annotation { "Feature Type Name" : "Feature", "Feature Type Description" : "" }
export const myFeature = defineFeature(function(context is Context, id is Id, definition is map)
    precondition{}
    {
        {
            var Q0;
            Q0=qCreatedBy(makeId("Top.planeOp"),FACE);
            var sketch = newSketch(context, id + "F0", { "sketchPlane" : qUnion([Q0])});
            skLineSegment(sketch, "E0.bottom", {"start": v(65.08, 7.73) * mm, "end": v(-14.92, 7.73) * mm});
            skLineSegment(sketch, "E0.top", {"start": v(65.08, 9.73) * mm, "end": v(-14.92, 9.73) * mm});
            skLineSegment(sketch, "E0.left", {"start": v(65.08, 7.73) * mm, "end": v(65.08, 9.73) * mm});
            skLineSegment(sketch, "E0.right", {"start": v(-14.92, 7.73) * mm, "end": v(-14.92, 9.73) * mm});
            skLineSegment(sketch, "E1", {"start": v(65.08, 9.73) * mm, "end": v(67.86, 29.54) * mm});
            skLineSegment(sketch, "E2", {"start": v(67.86, 29.54) * mm, "end": v(63.86, 29.54) * mm});
            skLineSegment(sketch, "E3", {"start": v(63.86, 29.54) * mm, "end": v(61.77, 14.68) * mm});
            skLineSegment(sketch, "E4", {"start": v(61.77, 14.68) * mm, "end": v(59.77, 14.68) * mm});
            skLineSegment(sketch, "E5", {"start": v(59.77, 14.68) * mm, "end": v(61.3, 25.58) * mm});
            skLineSegment(sketch, "E6", {"start": v(61.3, 25.58) * mm, "end": v(57.3, 25.58) * mm});
            skLineSegment(sketch, "E7", {"start": v(57.3, 25.58) * mm, "end": v(55.77, 14.68) * mm});
            skLineSegment(sketch, "E8", {"start": v(55.77, 14.68) * mm, "end": v(53.77, 14.68) * mm});
            skLineSegment(sketch, "E9", {"start": v(53.77, 14.68) * mm, "end": v(55.77, 29.54) * mm});
            skLineSegment(sketch, "E10", {"start": v(55.77, 29.54) * mm, "end": v(51.77, 29.54) * mm});
            skLineSegment(sketch, "E11", {"start": v(51.77, 29.54) * mm, "end": v(49, 9.73) * mm});
            skLineSegment(sketch, "E12", {"start": v(46.97, 9.73) * mm, "end": v(49.76, 29.54) * mm});
            skLineSegment(sketch, "E13", {"start": v(49.76, 29.54) * mm, "end": v(33.76, 29.54) * mm});
            skLineSegment(sketch, "E14", {"start": v(33.76, 29.54) * mm, "end": v(30.97, 9.73) * mm});
            skLineSegment(sketch, "E15", {"start": v(37.23, 25.54) * mm, "end": v(45.15, 25.54) * mm});
            skLineSegment(sketch, "E16", {"start": v(45.15, 25.54) * mm, "end": v(43.5, 13.73) * mm});
            skLineSegment(sketch, "E17", {"start": v(43.5, 13.73) * mm, "end": v(35.57, 13.73) * mm});
            skLineSegment(sketch, "E18", {"start": v(37.23, 25.54) * mm, "end": v(35.57, 13.73) * mm});
            skLineSegment(sketch, "E19", {"start": v(65.08, 9.73) * mm, "end": v(49, 9.73) * mm});
            skLineSegment(sketch, "E20", {"start": v(46.97, 9.73) * mm, "end": v(30.97, 9.73) * mm});
            skLineSegment(sketch, "E21", {"start": v(12.8, 9.73) * mm, "end": v(15.58, 29.54) * mm});
            skLineSegment(sketch, "E22", {"start": v(15.58, 29.54) * mm, "end": v(19.58, 29.54) * mm});
            skLineSegment(sketch, "E23", {"start": v(19.58, 29.54) * mm, "end": v(17.35, 13.7) * mm});
            skLineSegment(sketch, "E24", {"start": v(17.35, 13.7) * mm, "end": v(29.5, 13.7) * mm});
            skLineSegment(sketch, "E25", {"start": v(29.5, 13.7) * mm, "end": v(28.95, 9.73) * mm});
            skLineSegment(sketch, "E26", {"start": v(0, 17.54) * mm, "end": v(-1.1, 9.73) * mm});
            skLineSegment(sketch, "E27", {"start": v(13.58, 29.54) * mm, "end": v(13.02, 25.54) * mm});
            skLineSegment(sketch, "E28", {"start": v(-2.35, 29.54) * mm, "end": v(13.58, 29.54) * mm});
            skLineSegment(sketch, "E29", {"start": v(0.56, 21.54) * mm, "end": v(6.56, 21.54) * mm});
            skLineSegment(sketch, "E30", {"start": v(0, 17.54) * mm, "end": v(6, 17.54) * mm});
            skLineSegment(sketch, "E31", {"start": v(6, 17.54) * mm, "end": v(6.56, 21.54) * mm});
            skLineSegment(sketch, "E32", {"start": v(0.56, 21.54) * mm, "end": v(1.12, 25.54) * mm});
            skLineSegment(sketch, "E33", {"start": v(1.12, 25.54) * mm, "end": v(13.02, 25.54) * mm});
            skLineSegment(sketch, "E34", {"start": v(-2.35, 29.54) * mm, "end": v(-5.14, 9.73) * mm});
            skSolve(sketch);
        }
        {
            var Q0;
            Q0 = qSketchRegion(id + "F0", true);
            extrude(context, id + "F1", {"entities" : qUnion([Q0]), "oppositeDirection" : true, "depth" : 5 * mm});
        }
        {
            var Q0;
            Q0=qCreatedBy(makeId("Top.planeOp"),FACE);
            var sketch = newSketch(context, id + "F2", { "sketchPlane" : qUnion([Q0])});
            skLineSegment(sketch, "E35", {"start": v(-14.7, 10.84) * mm, "end": v(-11.55, 29.48) * mm});
            skLineSegment(sketch, "E36", {"start": v(-11.55, 29.48) * mm, "end": v(-12.91, 10.27) * mm});
            skLineSegment(sketch, "E37", {"start": v(-12.91, 10.27) * mm, "end": v(-6.82, 20.75) * mm});
            skLineSegment(sketch, "E38", {"start": v(-6.82, 20.75) * mm, "end": v(-11.55, 9.46) * mm});
            skLineSegment(sketch, "E39", {"start": v(-11.55, 9.46) * mm, "end": v(-4.86, 14.96) * mm});
            skLineSegment(sketch, "E40", {"start": v(-4.86, 14.96) * mm, "end": v(-11.71, 8.56) * mm});
            skLineSegment(sketch, "E41", {"start": v(-11.84, 7.2) * mm, "end": v(2.06, -2.1) * mm});
            skLineSegment(sketch, "E42", {"start": v(2.06, -2.1) * mm, "end": v(-13.52, 7.02) * mm});
            skLineSegment(sketch, "E43", {"start": v(-13.52, 7.02) * mm, "end": v(-12.77, 1.13) * mm});
            skLineSegment(sketch, "E44", {"start": v(-12.77, 1.13) * mm, "end": v(-14.73, 7.2) * mm});
            skLineSegment(sketch, "E45", {"start": v(-14.73, 7.2) * mm, "end": v(-24.38, -5.63) * mm});
            skLineSegment(sketch, "E46", {"start": v(-24.38, -5.63) * mm, "end": v(-15.5, 8.52) * mm});
            skLineSegment(sketch, "E47", {"start": v(-15.5, 8.52) * mm, "end": v(-24.38, 7.02) * mm});
            skLineSegment(sketch, "E48", {"start": v(-17.63, 10.08) * mm, "end": v(-15.5, 10.08) * mm});
            skLineSegment(sketch, "E49", {"start": v(-11.84, 7.2) * mm, "end": v(-0.95, 9.17) * mm});
            skLineSegment(sketch, "E50", {"start": v(-0.95, 9.17) * mm, "end": v(-11.71, 8.56) * mm});
            skLineSegment(sketch, "E51", {"start": v(-24.38, 7.02) * mm, "end": v(-15.54, 9.15) * mm});
            skLineSegment(sketch, "E52", {"start": v(-15.54, 9.15) * mm, "end": v(-17.63, 10.08) * mm});
            skLineSegment(sketch, "E53", {"start": v(-15.5, 10.08) * mm, "end": v(-23.35, 18.2) * mm});
            skLineSegment(sketch, "E54", {"start": v(-23.35, 18.2) * mm, "end": v(-14.7, 10.84) * mm});
            skSolve(sketch);
        }
        {
            var Q0;
            Q0 = qSketchRegion(id + "F2", true);
            extrude(context, id + "F3", {"entities" : qUnion([Q0]), "operationType" : NewBodyOperationType.ADD, "oppositeDirection" : true, "depth" : 5 * mm, "hasSecondDirection" : true, "secondDirectionOppositeDirection" : false, "secondDirectionDepth" : 4 * mm});
        }
        {
            var Q0;
            Q0=makeQuery(id+"F0.imprint","IMPRINT",FACE,{"disambiguationData":[TD([[makeQuery(id+"F0.imprint","IMPRINT",EDGE,{"derivedFrom":sQuery(id+"F0.wireOp",EDGE,"E0.bottom")}),-1.0]])]});
            extrude(context, id + "F4", {"entities" : qUnion([Q0]), "operationType" : NewBodyOperationType.ADD, "depth" : 2 * mm});
        }
        {
            var Q0;
            {var subQ0=sQuery(id+"F0.wireOp",EDGE,"E29");var subQ2=sQuery(id+"F0.wireOp",EDGE,"E28");var subQ4=sQuery(id+"F0.wireOp",EDGE,"E27");var subQ6=sQuery(id+"F0.wireOp",EDGE,"E26");var subQ7=makeQuery(id+"F1.opExtrude","SWEPT_FACE",FACE,{"disambiguationData":[OSD([subQ6])]});var subQ8=sQuery(id+"F0.wireOp",EDGE,"E30");var subQ11=sQuery(id+"F0.wireOp",EDGE,"E11");var subQ12=sQuery(id+"F0.wireOp",EDGE,"E0.top");var subQ14=sQuery(id+"F0.wireOp",EDGE,"E12");var subQ16=sQuery(id+"F0.wireOp",EDGE,"E31");var subQ18=sQuery(id+"F0.wireOp",EDGE,"E14");var subQ19=sQuery(id+"F0.wireOp",EDGE,"E25");var subQ21=sQuery(id+"F0.wireOp",EDGE,"E21");var subQ23=sQuery(id+"F0.wireOp",EDGE,"E0.right");var subQ24=sQuery(id+"F0.wireOp",EDGE,"E34");var subQ26=sQuery(id+"F0.wireOp",EDGE,"E32");var subQ28=sQuery(id+"F0.wireOp",EDGE,"E33");var subQ31=sQuery(id+"F0.wireOp",EDGE,"E16");var subQ32=sQuery(id+"F0.wireOp",EDGE,"E13");var subQ33=sQuery(id+"F0.wireOp",EDGE,"E10");var subQ34=sQuery(id+"F0.wireOp",EDGE,"E9");var subQ35=sQuery(id+"F0.wireOp",EDGE,"E8");var subQ36=sQuery(id+"F0.wireOp",EDGE,"E7");var subQ37=sQuery(id+"F0.wireOp",EDGE,"E6");var subQ38=sQuery(id+"F0.wireOp",EDGE,"E5");var subQ39=sQuery(id+"F0.wireOp",EDGE,"E15");var subQ40=sQuery(id+"F0.wireOp",EDGE,"E0.bottom");var subQ41=sQuery(id+"F0.wireOp",EDGE,"E3");var subQ42=sQuery(id+"F0.wireOp",EDGE,"E0.left");var subQ43=sQuery(id+"F0.wireOp",EDGE,"E1");var subQ44=sQuery(id+"F0.wireOp",EDGE,"E2");var subQ45=sQuery(id+"F0.wireOp",EDGE,"E4");var subQ46=sQuery(id+"F0.wireOp",EDGE,"E17");var subQ47=sQuery(id+"F0.wireOp",EDGE,"E18");var subQ48=sQuery(id+"F0.wireOp",EDGE,"E22");var subQ49=sQuery(id+"F0.wireOp",EDGE,"E23");var subQ50=sQuery(id+"F0.wireOp",EDGE,"E24");Q0=makeQuery(id+"F4.boolean.opBoolean","SPLIT",FACE,{"disambiguationData":[TD([subQ7])],"derivedFrom":makeQuery(id+"F3.boolean.opBoolean","SPLIT",FACE,{"disambiguationData":[TD([makeQuery(id+"F1.opExtrude","SWEPT_FACE",FACE,{"disambiguationData":[OSD([subQ40])]})])],"derivedFrom":makeQuery(id+"F1.opExtrude","CAP_FACE",FACE,{"disambiguationData":[OSD([subQ40,subQ12,subQ42,subQ23,subQ43,subQ44,subQ41,subQ45,subQ38,subQ37,subQ36,subQ35,subQ34,subQ33,subQ11,subQ14,subQ32,subQ18,subQ39,subQ31,subQ46,subQ47,subQ21,subQ48,subQ49,subQ50,subQ19,subQ6,subQ4,subQ2,subQ0,subQ8,subQ16,subQ26,subQ28,subQ24])],"isStart":true})})});}
            var sketch = newSketch(context, id + "F5", { "sketchPlane" : qUnion([Q0])});
            skText(sketch, "E55", { "text": "Flexible Orientation Welding", "fontName": "OpenSans-Italic.ttf"});
            const initialGuessF5  = {"E55": [-0.0049, 0.00297, 1, 0, 0.00376]};
            skSetInitialGuess(sketch, initialGuessF5);
            skSolve(sketch);
        }
        {
            var Q0;
            Q0 = qSketchRegion(id + "F5", true);
            extrude(context, id + "F6", {"entities" : qUnion([Q0]), "oppositeDirection" : true, "depth" : 5 * mm});
        }
        {
            var Q0;
            Q0=makeQuery(id+"F3.boolean.opBoolean","MERGE",FACE,{"derivedFrom":[makeQuery(id+"F1.opExtrude","CAP_FACE",FACE,{"disambiguationData":[OSD([sQuery(id+"F0.wireOp",EDGE,"E0.bottom"),sQuery(id+"F0.wireOp",EDGE,"E0.top"),sQuery(id+"F0.wireOp",EDGE,"E0.left"),sQuery(id+"F0.wireOp",EDGE,"E0.right"),sQuery(id+"F0.wireOp",EDGE,"E1"),sQuery(id+"F0.wireOp",EDGE,"E2"),sQuery(id+"F0.wireOp",EDGE,"E3"),sQuery(id+"F0.wireOp",EDGE,"E4"),sQuery(id+"F0.wireOp",EDGE,"E5"),sQuery(id+"F0.wireOp",EDGE,"E6"),sQuery(id+"F0.wireOp",EDGE,"E7"),sQuery(id+"F0.wireOp",EDGE,"E8"),sQuery(id+"F0.wireOp",EDGE,"E9"),sQuery(id+"F0.wireOp",EDGE,"E10"),sQuery(id+"F0.wireOp",EDGE,"E11"),sQuery(id+"F0.wireOp",EDGE,"E12"),sQuery(id+"F0.wireOp",EDGE,"E13"),sQuery(id+"F0.wireOp",EDGE,"E14"),sQuery(id+"F0.wireOp",EDGE,"E15"),sQuery(id+"F0.wireOp",EDGE,"E16"),sQuery(id+"F0.wireOp",EDGE,"E17"),sQuery(id+"F0.wireOp",EDGE,"E18"),sQuery(id+"F0.wireOp",EDGE,"E21"),sQuery(id+"F0.wireOp",EDGE,"E22"),sQuery(id+"F0.wireOp",EDGE,"E23"),sQuery(id+"F0.wireOp",EDGE,"E24"),sQuery(id+"F0.wireOp",EDGE,"E25"),sQuery(id+"F0.wireOp",EDGE,"E26"),sQuery(id+"F0.wireOp",EDGE,"E27"),sQuery(id+"F0.wireOp",EDGE,"E28"),sQuery(id+"F0.wireOp",EDGE,"E29"),sQuery(id+"F0.wireOp",EDGE,"E30"),sQuery(id+"F0.wireOp",EDGE,"E31"),sQuery(id+"F0.wireOp",EDGE,"E32"),sQuery(id+"F0.wireOp",EDGE,"E33"),sQuery(id+"F0.wireOp",EDGE,"E34")])],"isStart":false}),makeQuery(id+"F3.opExtrude","CAP_FACE",FACE,{"disambiguationData":[OSD([sQuery(id+"F2.wireOp",EDGE,"E35"),sQuery(id+"F2.wireOp",EDGE,"E36"),sQuery(id+"F2.wireOp",EDGE,"E37"),sQuery(id+"F2.wireOp",EDGE,"E38"),sQuery(id+"F2.wireOp",EDGE,"E39"),sQuery(id+"F2.wireOp",EDGE,"E40"),sQuery(id+"F2.wireOp",EDGE,"E41"),sQuery(id+"F2.wireOp",EDGE,"E42"),sQuery(id+"F2.wireOp",EDGE,"E43"),sQuery(id+"F2.wireOp",EDGE,"E44"),sQuery(id+"F2.wireOp",EDGE,"E45"),sQuery(id+"F2.wireOp",EDGE,"E46"),sQuery(id+"F2.wireOp",EDGE,"E47"),sQuery(id+"F2.wireOp",EDGE,"E48"),sQuery(id+"F2.wireOp",EDGE,"E49"),sQuery(id+"F2.wireOp",EDGE,"E50"),sQuery(id+"F2.wireOp",EDGE,"E51"),sQuery(id+"F2.wireOp",EDGE,"E52"),sQuery(id+"F2.wireOp",EDGE,"E53"),sQuery(id+"F2.wireOp",EDGE,"E54")])],"isStart":false})]});
            var sketch = newSketch(context, id + "F7", { "sketchPlane" : qUnion([Q0])});
            skLineSegment(sketch, "E56.bottom", {"start": v(-28.1, 10.02) * mm, "end": v(73.5, 10.02) * mm});
            skLineSegment(sketch, "E56.top", {"start": v(-28.1, -40.78) * mm, "end": v(73.5, -40.78) * mm});
            skLineSegment(sketch, "E56.left", {"start": v(-28.1, 10.02) * mm, "end": v(-28.1, -40.78) * mm});
            skLineSegment(sketch, "E56.right", {"start": v(73.5, 10.02) * mm, "end": v(73.5, -40.78) * mm});
            skSolve(sketch);
        }
        {
            var Q0;
            Q0 = qSketchRegion(id + "F7", true);
            extrude(context, id + "F8", {"entities" : qUnion([Q0]), "depth" : 3 * mm});
        }
    });